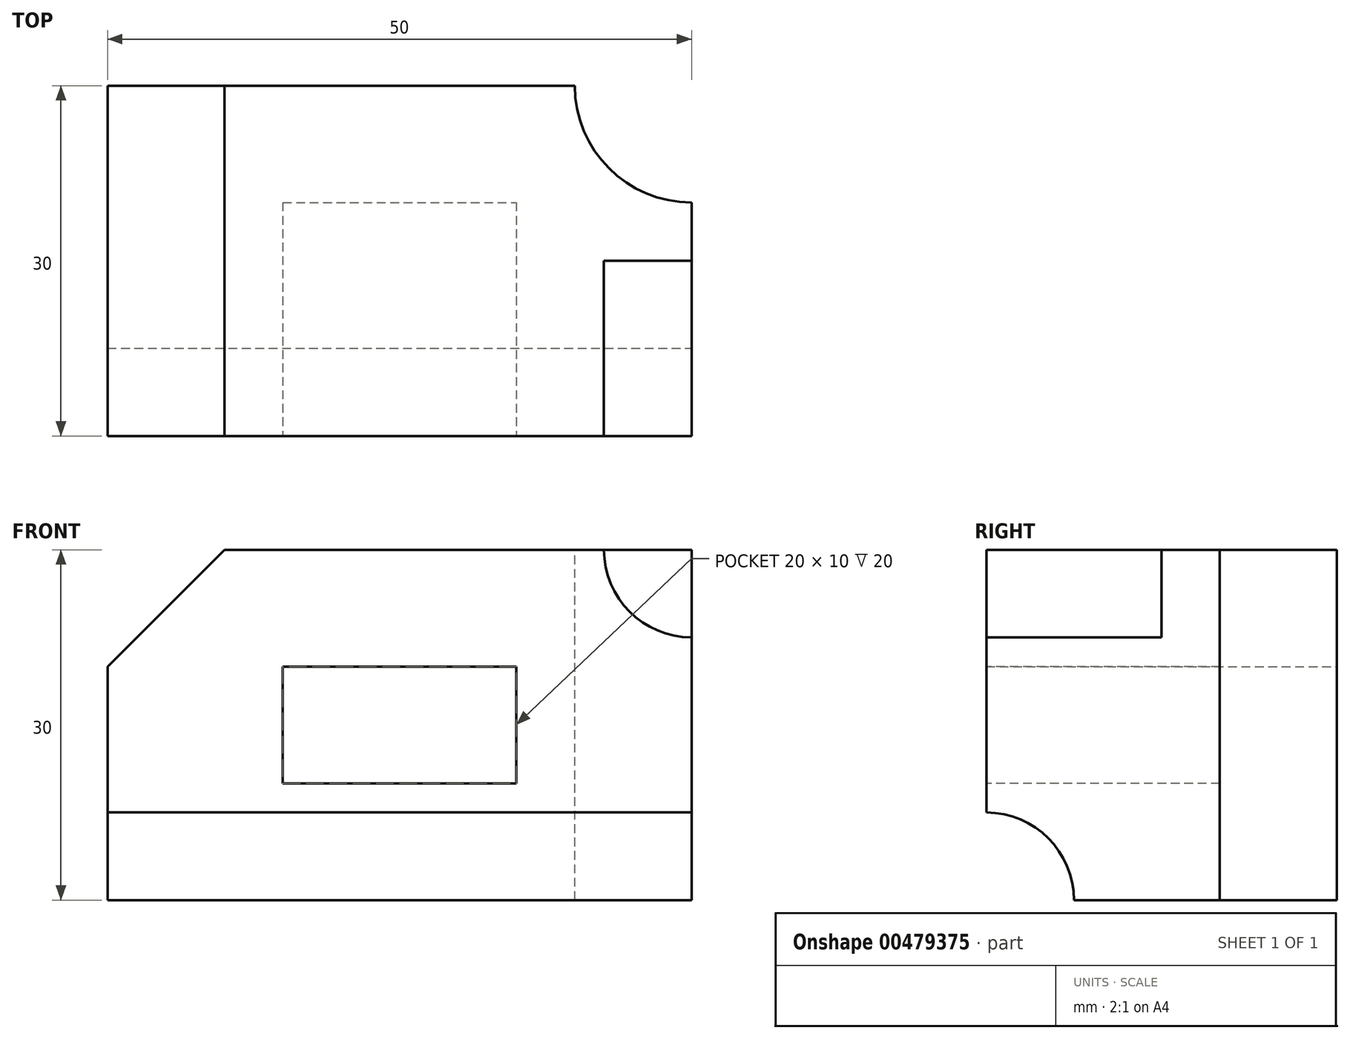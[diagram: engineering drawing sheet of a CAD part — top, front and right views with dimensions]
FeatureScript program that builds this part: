
annotation { "Feature Type Name" : "Feature", "Feature Type Description" : "" }
export const myFeature = defineFeature(function(context is Context, id is Id, definition is map)
    precondition{}
    {
        {
            var Q0;
            Q0=qCreatedBy(makeId("Front.planeOp"),FACE);
            var sketch = newSketch(context, id + "F0", { "sketchPlane" : qUnion([Q0])});
            skLineSegment(sketch, "E0.bottom", {"start": v(0, 0) * mm, "end": v(50, 0) * mm});
            skLineSegment(sketch, "E0.top", {"start": v(0, 30) * mm, "end": v(50, 30) * mm});
            skLineSegment(sketch, "E0.left", {"start": v(0, 0) * mm, "end": v(0, 30) * mm});
            skLineSegment(sketch, "E0.right", {"start": v(50, 0) * mm, "end": v(50, 30) * mm});
            skSolve(sketch);
        }
        {
            var Q0;
            Q0 = qSketchRegion(id + "F0", true);
            extrude(context, id + "F1", {"entities" : qUnion([Q0]), "depth" : 30 * mm});
        }
        {
            var Q0;
            Q0=makeQuery(id+"F1.opExtrude","SWEPT_EDGE",EDGE,{"disambiguationData":[OSD([sQuery(id+"F0.wireOp",EDGE,"E0.top"),sQuery(id+"F0.wireOp",EDGE,"E0.left")])]});
            chamfer(context, id + "F2", {"entities" : qUnion([Q0]), "width" : 10 * mm, "tangentPropagation" : true});
        }
        {
            var Q0;
            Q0=makeQuery(id+"F1.opExtrude","SWEPT_FACE",FACE,{"disambiguationData":[OSD([sQuery(id+"F0.wireOp",EDGE,"E0.top")])]});
            var sketch = newSketch(context, id + "F3", { "sketchPlane" : qUnion([Q0])});
            skCircle(sketch, "E1", {"center": v(50, 0) * mm, "radius": 10 * mm});
            skSolve(sketch);
        }
        {
            var Q0;
            Q0 = qSketchRegion(id + "F3", true);
            extrude(context, id + "F4", {"entities" : qUnion([Q0]), "operationType" : NewBodyOperationType.REMOVE, "endBound" : BoundingType.THROUGH_ALL, "oppositeDirection" : true, "depth" : 25 * mm});
        }
        {
            var Q0;
            Q0=makeQuery(id+"F1.opExtrude","SWEPT_FACE",FACE,{"disambiguationData":[OSD([sQuery(id+"F0.wireOp",EDGE,"E0.right")])]});
            var sketch = newSketch(context, id + "F5", { "sketchPlane" : qUnion([Q0])});
            skCircle(sketch, "E2", {"center": v(-30, 0) * mm, "radius": 7.5 * mm});
            skSolve(sketch);
        }
        {
            var Q0;
            Q0 = qSketchRegion(id + "F5", true);
            extrude(context, id + "F6", {"entities" : qUnion([Q0]), "operationType" : NewBodyOperationType.REMOVE, "endBound" : BoundingType.THROUGH_ALL, "oppositeDirection" : true, "depth" : 25 * mm});
        }
        {
            var Q0;
            Q0=makeQuery(id+"F1.opExtrude","CAP_FACE",FACE,{"disambiguationData":[OSD([sQuery(id+"F0.wireOp",EDGE,"E0.bottom"),sQuery(id+"F0.wireOp",EDGE,"E0.top"),sQuery(id+"F0.wireOp",EDGE,"E0.left"),sQuery(id+"F0.wireOp",EDGE,"E0.right")])],"isStart":false});
            var sketch = newSketch(context, id + "F7", { "sketchPlane" : qUnion([Q0])});
            skCircle(sketch, "E3", {"center": v(50, 30) * mm, "radius": 7.5 * mm});
            skSolve(sketch);
        }
        {
            var Q0;
            Q0 = qSketchRegion(id + "F7", true);
            extrude(context, id + "F8", {"entities" : qUnion([Q0]), "operationType" : NewBodyOperationType.REMOVE, "oppositeDirection" : true, "depth" : 15 * mm});
        }
        {
            var Q0;
            Q0=makeQuery(id+"F1.opExtrude","CAP_FACE",FACE,{"disambiguationData":[OSD([sQuery(id+"F0.wireOp",EDGE,"E0.bottom"),sQuery(id+"F0.wireOp",EDGE,"E0.top"),sQuery(id+"F0.wireOp",EDGE,"E0.left"),sQuery(id+"F0.wireOp",EDGE,"E0.right")])],"isStart":false});
            var sketch = newSketch(context, id + "F9", { "sketchPlane" : qUnion([Q0])});
            skLineSegment(sketch, "E4.bottom", {"start": v(15, 20) * mm, "end": v(35, 20) * mm});
            skLineSegment(sketch, "E4.top", {"start": v(15, 10) * mm, "end": v(35, 10) * mm});
            skLineSegment(sketch, "E4.left", {"start": v(15, 20) * mm, "end": v(15, 10) * mm});
            skLineSegment(sketch, "E4.right", {"start": v(35, 20) * mm, "end": v(35, 10) * mm});
            skSolve(sketch);
        }
        {
            var Q0;
            Q0 = qSketchRegion(id + "F9", true);
            extrude(context, id + "F10", {"entities" : qUnion([Q0]), "operationType" : NewBodyOperationType.REMOVE, "oppositeDirection" : true, "depth" : 20 * mm});
        }
    });
